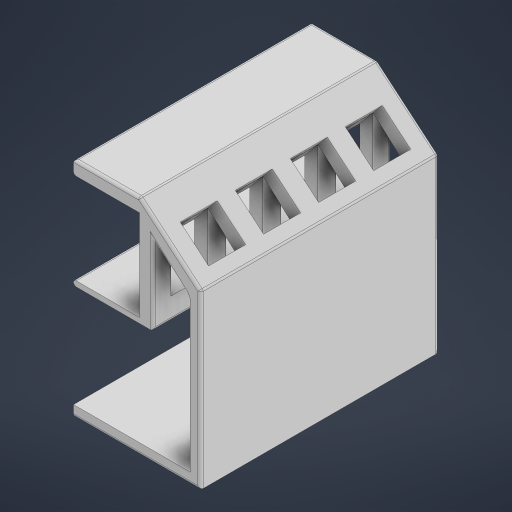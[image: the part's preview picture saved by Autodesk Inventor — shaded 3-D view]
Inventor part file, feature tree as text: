
AUTODESK INVENTOR PART (.ipt)
format: ipt  version: 2024 (Build 280153000, 153)  size: 318,976 bytes
history: native  units: mm
features: extrude x2, move_body x2, sketch x2, fillet x1
ambient origin geometry x8: Origin, YZ Plane, XZ Plane, XY Plane, X Axis, Y Axis, Z Axis, Center Point
bodies: Solid1 (feature_tree)
feature tree (7):
  extrude  "Extrusion1"  Depth=25.0mm
  extrude  "Extrusion2"  Depth=5.0mm
  move_body  "Move Body1"
  move_body  "Move Body2"
  fillet  "Fillet1"  Radius=30.0mm
  sketch  "Sketch1"  dims[d0=34.25mm d1=25.0mm]
  sketch  "Sketch2"  dims[d2=25.0mm d3=5.0mm d4=30.0mm d5=22.68928mm d6=6.0mm d7=5.0mm d8=2.0mm d9=90.0mm d10=0.0mm d11=14.0mm d12=14.0mm d13=14.0mm d14=14.0mm d15=14.0mm d16=14.0mm d17=14.0mm d18=14.0mm d19=6.8mm d20=6.8mm d21=6.8mm d22=6.8mm d23=90.0mm d24=0.0mm d25=90.0deg d26=270.0deg d27=1.0mm d28=65.0mm d29=4.0mm]
